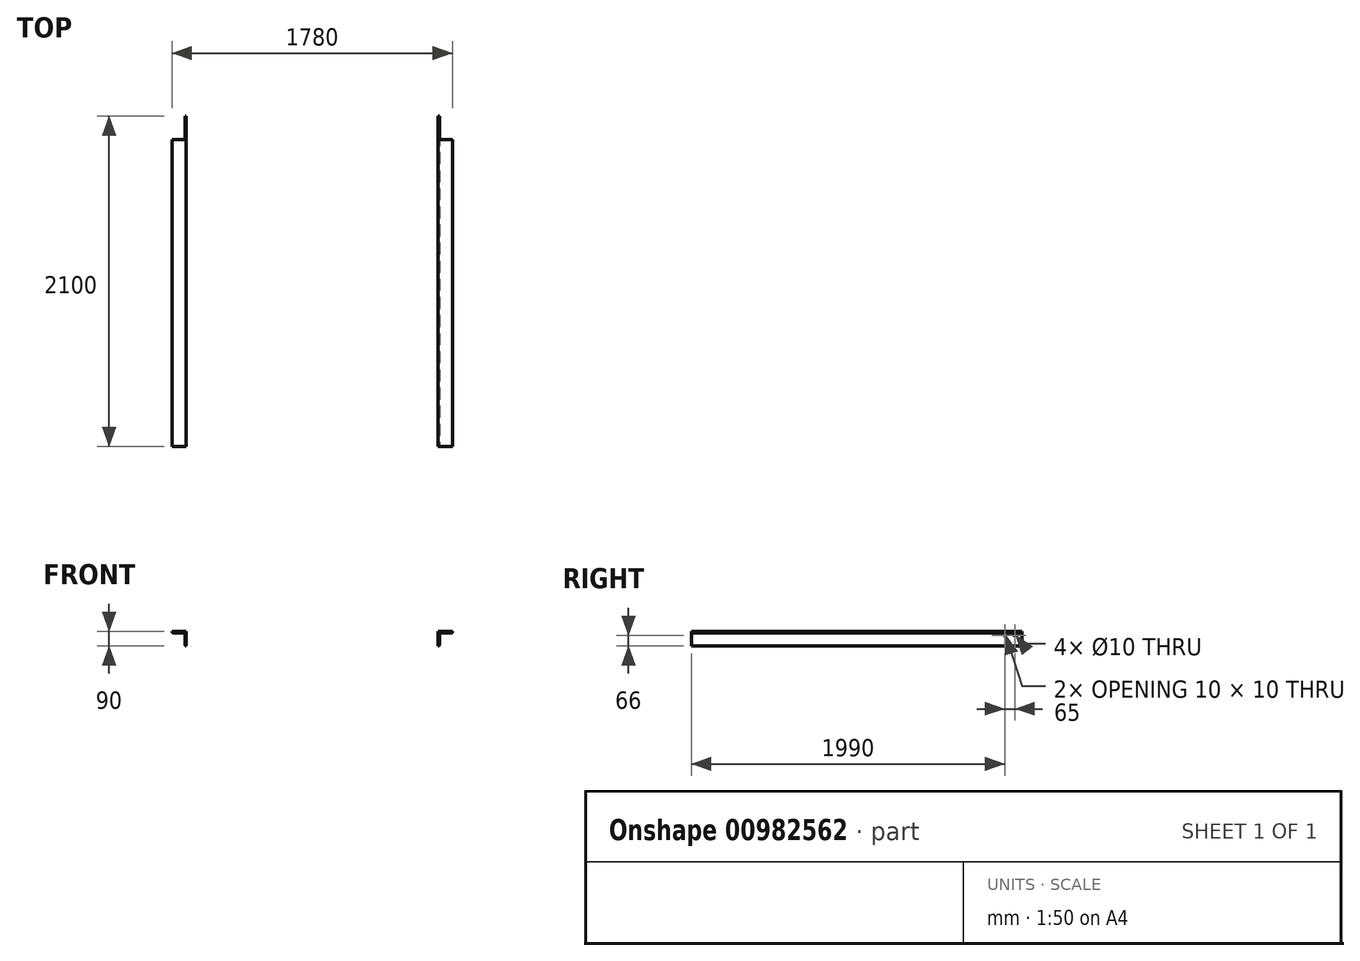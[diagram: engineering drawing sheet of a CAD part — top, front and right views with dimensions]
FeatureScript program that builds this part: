
annotation { "Feature Type Name" : "Feature", "Feature Type Description" : "" }
export const myFeature = defineFeature(function(context is Context, id is Id, definition is map)
    precondition{}
    {
        {
            var Q0;
            Q0=qCreatedBy(makeId("Front.planeOp"),FACE);
            var sketch = newSketch(context, id + "F0", { "sketchPlane" : qUnion([Q0])});
            skLineSegment(sketch, "E0", {"start": v(0, 0) * mm, "end": v(90, 0) * mm});
            skLineSegment(sketch, "E1", {"start": v(0, 0) * mm, "end": v(0, -90) * mm});
            skLineSegment(sketch, "E2", {"start": v(0, -90) * mm, "end": v(3, -90) * mm});
            skLineSegment(sketch, "E3", {"start": v(7, -86) * mm, "end": v(7, -11) * mm});
            skLineSegment(sketch, "E4", {"start": v(11, -7) * mm, "end": v(86, -7) * mm});
            skLineSegment(sketch, "E5", {"start": v(90, -3) * mm, "end": v(90, 0) * mm});
            skPoint(sketch, "E6.visualSharp", {"position": v(90, -7) * mm});
            skArc(sketch, "E6.filletArc", {"start": v(86, -7) * mm, "mid": v(88.83, -5.83) * mm, "end": v(90, -3) * mm});
            skPoint(sketch, "E7.visualSharp", {"position": v(7, -7) * mm});
            skArc(sketch, "E7.filletArc", {"start": v(11, -7) * mm, "mid": v(8.17, -8.17) * mm, "end": v(7, -11) * mm});
            skPoint(sketch, "E8.visualSharp", {"position": v(7, -90) * mm});
            skArc(sketch, "E8.filletArc", {"start": v(3, -90) * mm, "mid": v(5.83, -88.83) * mm, "end": v(7, -86) * mm});
            skSolve(sketch);
        }
        {
            var Q0;
            Q0 = qSketchRegion(id + "F0", true);
            extrude(context, id + "F1", {"entities" : qUnion([Q0]), "depth" : -2100 * mm, "offsetDistance" : 25 * mm});
        }
        {
            var Q0;
            Q0=makeQuery(id+"F1.opExtrude","SWEPT_FACE",FACE,{"disambiguationData":[OSD([sQuery(id+"F0.wireOp",EDGE,"E0")])]});
            var sketch = newSketch(context, id + "F2", { "sketchPlane" : qUnion([Q0])});
            skLineSegment(sketch, "E9.bottom", {"start": v(98, 1950) * mm, "end": v(8, 1950) * mm});
            skLineSegment(sketch, "E9.top", {"start": v(98, 2100) * mm, "end": v(8, 2100) * mm});
            skLineSegment(sketch, "E9.left", {"start": v(98, 1950) * mm, "end": v(98, 2100) * mm});
            skLineSegment(sketch, "E9.right", {"start": v(8, 1950) * mm, "end": v(8, 2100) * mm});
            skSolve(sketch);
        }
        {
            var Q0;
            Q0 = qSketchRegion(id + "F2", true);
            extrude(context, id + "F3", {"entities" : qUnion([Q0]), "operationType" : NewBodyOperationType.REMOVE, "oppositeDirection" : true, "depth" : 25 * mm, "offsetDistance" : 25 * mm});
        }
        {
            var Q0;
            Q0=makeQuery(id+"F1.opExtrude","SWEPT_FACE",FACE,{"disambiguationData":[OSD([sQuery(id+"F0.wireOp",EDGE,"E1")])]});
            var sketch = newSketch(context, id + "F4", { "sketchPlane" : qUnion([Q0])});
            skPoint(sketch, "E10", {"position": v(-2055, -24) * mm});
            skPoint(sketch, "E11", {"position": v(-1990, -24) * mm});
            skSolve(sketch);
        }
        {
            var Q0;
            Q0=sQuery(id+"F4.wireOp",VERTEX,"E10");
            var Q1;
            Q1=sQuery(id+"F4.wireOp",VERTEX,"E11");
            var Q2;
            Q2=makeQuery(id+"F1.opExtrude","SWEPT_BODY",BODY,{"disambiguationData":[OSD([sQuery(id+"F0.wireOp",EDGE,"E0"),sQuery(id+"F0.wireOp",EDGE,"E1"),sQuery(id+"F0.wireOp",EDGE,"E2"),sQuery(id+"F0.wireOp",EDGE,"E3"),sQuery(id+"F0.wireOp",EDGE,"E4"),sQuery(id+"F0.wireOp",EDGE,"E5"),sQuery(id+"F0.wireOp",EDGE,"E6.filletArc"),sQuery(id+"F0.wireOp",EDGE,"E7.filletArc"),sQuery(id+"F0.wireOp",EDGE,"E8.filletArc")])]});
            hole(context, id + "F5", {"style" : HoleStyle.C_SINK, "endStyle" : HoleEndStyle.BLIND, "holeDiameter" : 10 * mm, "cSinkDiameter" : 12 * mm, "cSinkAngle" : 90 * degree, "majorDiameter" : 5 * mm, "holeDepth" : 30 * mm, "isTappedThrough" : true, "tappedDepth" : 4 * mm, "tapClearance" : 3, "startFromSketch" : true, "locations" : qUnion([Q0, Q1]), "scope" : qUnion([Q2])});
        }
        {
            var Q0;
            Q0=qCreatedBy(makeId("Right.planeOp"),FACE);
            cPlane(context, id + "F6", {"entities" : qUnion([Q0]), "cplaneType" : CPlaneType.OFFSET, "offset" : 800 * mm, "oppositeDirection" : true, "width" : 150 * mm, "height" : 150 * mm});
        }
        {
            var Q0;
            Q0=makeQuery(id+"F1.opExtrude","SWEPT_BODY",BODY,{"disambiguationData":[OSD([sQuery(id+"F0.wireOp",EDGE,"E0"),sQuery(id+"F0.wireOp",EDGE,"E1"),sQuery(id+"F0.wireOp",EDGE,"E2"),sQuery(id+"F0.wireOp",EDGE,"E3"),sQuery(id+"F0.wireOp",EDGE,"E4"),sQuery(id+"F0.wireOp",EDGE,"E5"),sQuery(id+"F0.wireOp",EDGE,"E6.filletArc"),sQuery(id+"F0.wireOp",EDGE,"E7.filletArc"),sQuery(id+"F0.wireOp",EDGE,"E8.filletArc")])]});
            var Q1;
            Q1=qCreatedBy(id+"F6.planeOp",FACE);
            mirror(context, id + "F7", {"entities" : qUnion([Q0]), "mirrorPlane" : qUnion([Q1])});
        }
    });
